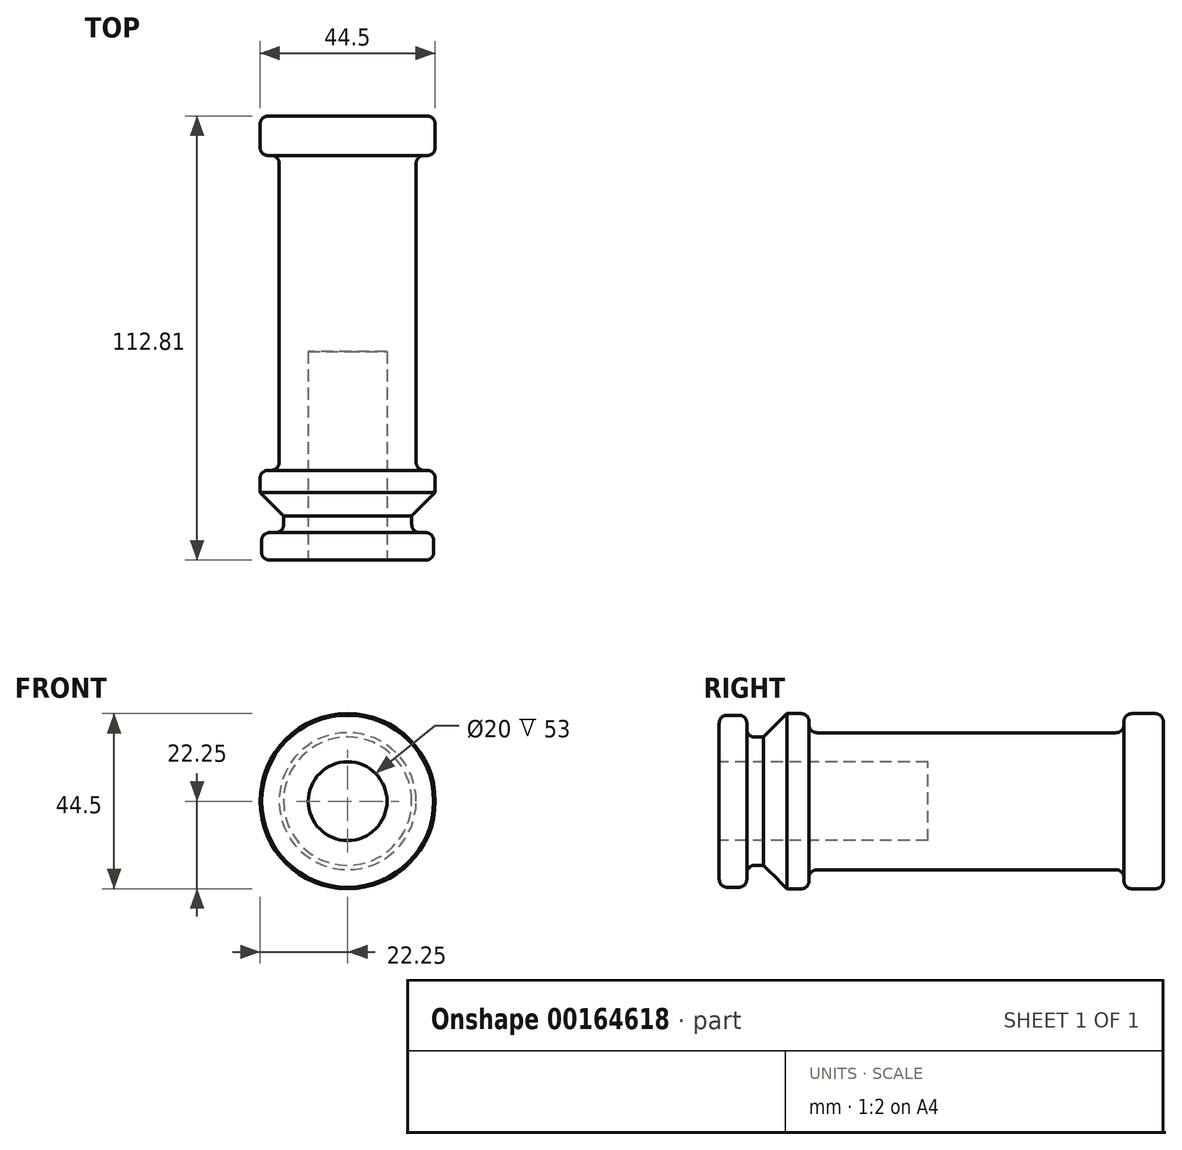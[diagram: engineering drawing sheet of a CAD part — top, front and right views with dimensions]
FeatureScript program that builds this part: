
annotation { "Feature Type Name" : "Feature", "Feature Type Description" : "" }
export const myFeature = defineFeature(function(context is Context, id is Id, definition is map)
    precondition{}
    {
        {
            var Q0;
            Q0=qCreatedBy(makeId("Right.planeOp"),FACE);
            var sketch = newSketch(context, id + "F0", { "sketchPlane" : qUnion([Q0])});
            skLineSegment(sketch, "E0", {"start": v(-45.97, 10) * mm, "end": v(-45.97, 19.86) * mm});
            skLineSegment(sketch, "E1", {"start": v(-43.97, 21.86) * mm, "end": v(-40.97, 21.86) * mm});
            skLineSegment(sketch, "E2", {"start": v(-38.97, 19.86) * mm, "end": v(-38.97, 18.3) * mm});
            skLineSegment(sketch, "E3", {"start": v(-36.97, 16.3) * mm, "end": v(-34.7, 16.3) * mm});
            skLineSegment(sketch, "E4", {"start": v(-34.7, 16.3) * mm, "end": v(-28.75, 22.25) * mm});
            skLineSegment(sketch, "E5", {"start": v(66.84, 20.25) * mm, "end": v(66.84, 0) * mm});
            skLineSegment(sketch, "E6", {"start": v(-28.75, 22.25) * mm, "end": v(-25.16, 22.25) * mm});
            skLineSegment(sketch, "E7", {"start": v(-23.16, 20.25) * mm, "end": v(-23.16, 19.41) * mm});
            skLineSegment(sketch, "E8", {"start": v(-21.16, 17.41) * mm, "end": v(54.84, 17.41) * mm});
            skLineSegment(sketch, "E9", {"start": v(56.84, 19.41) * mm, "end": v(56.84, 20.25) * mm});
            skLineSegment(sketch, "E10", {"start": v(58.84, 22.25) * mm, "end": v(64.84, 22.25) * mm});
            skLineSegment(sketch, "E11", {"start": v(-45.97, 10) * mm, "end": v(7.03, 10) * mm});
            skLineSegment(sketch, "E12", {"start": v(7.03, 10) * mm, "end": v(7.03, 0) * mm});
            skPoint(sketch, "E13.orphan", {"position": v(-45.97, 0) * mm});
            skLineSegment(sketch, "E14", {"start": v(7.03, 0) * mm, "end": v(66.84, 0) * mm});
            skPoint(sketch, "E15.visualSharp", {"position": v(-45.97, 21.86) * mm});
            skArc(sketch, "E15.filletArc", {"start": v(-43.97, 21.86) * mm, "mid": v(-45.39, 21.27) * mm, "end": v(-45.97, 19.86) * mm});
            skPoint(sketch, "E16.visualSharp", {"position": v(-38.97, 21.86) * mm});
            skArc(sketch, "E16.filletArc", {"start": v(-38.97, 19.86) * mm, "mid": v(-39.56, 21.27) * mm, "end": v(-40.97, 21.86) * mm});
            skPoint(sketch, "E17.visualSharp", {"position": v(-23.16, 17.41) * mm});
            skArc(sketch, "E17.filletArc", {"start": v(-23.16, 19.41) * mm, "mid": v(-22.57, 18) * mm, "end": v(-21.16, 17.41) * mm});
            skPoint(sketch, "E18.visualSharp", {"position": v(56.84, 17.41) * mm});
            skArc(sketch, "E18.filletArc", {"start": v(54.84, 17.41) * mm, "mid": v(56.25, 18) * mm, "end": v(56.84, 19.41) * mm});
            skPoint(sketch, "E19.visualSharp", {"position": v(56.84, 22.25) * mm});
            skArc(sketch, "E19.filletArc", {"start": v(58.84, 22.25) * mm, "mid": v(57.43, 21.67) * mm, "end": v(56.84, 20.25) * mm});
            skPoint(sketch, "E20.visualSharp", {"position": v(66.84, 22.25) * mm});
            skArc(sketch, "E20.filletArc", {"start": v(66.84, 20.25) * mm, "mid": v(66.25, 21.67) * mm, "end": v(64.84, 22.25) * mm});
            skPoint(sketch, "E21.visualSharp", {"position": v(-23.16, 22.25) * mm});
            skArc(sketch, "E21.filletArc", {"start": v(-23.16, 20.25) * mm, "mid": v(-23.75, 21.67) * mm, "end": v(-25.16, 22.25) * mm});
            skPoint(sketch, "E22.visualSharp", {"position": v(-38.97, 16.3) * mm});
            skArc(sketch, "E22.filletArc", {"start": v(-38.97, 18.3) * mm, "mid": v(-38.39, 16.88) * mm, "end": v(-36.97, 16.3) * mm});
            skLineSegment(sketch, "E23", {"start": v(-45.97, 0) * mm, "end": v(115.35, 0) * mm, "construction": true});
            skSolve(sketch);
        }
        {
            var Q0;
            Q0 = qSketchRegion(id + "F0", true);
            var Q1;
            Q1=sQuery(id+"F0.wireOp",EDGE,"E23");
            revolve(context, id + "F1", {"entities" : qUnion([Q0]), "axis" : qUnion([Q1]), "revolveType" : RevolveType.FULL});
        }
    });
